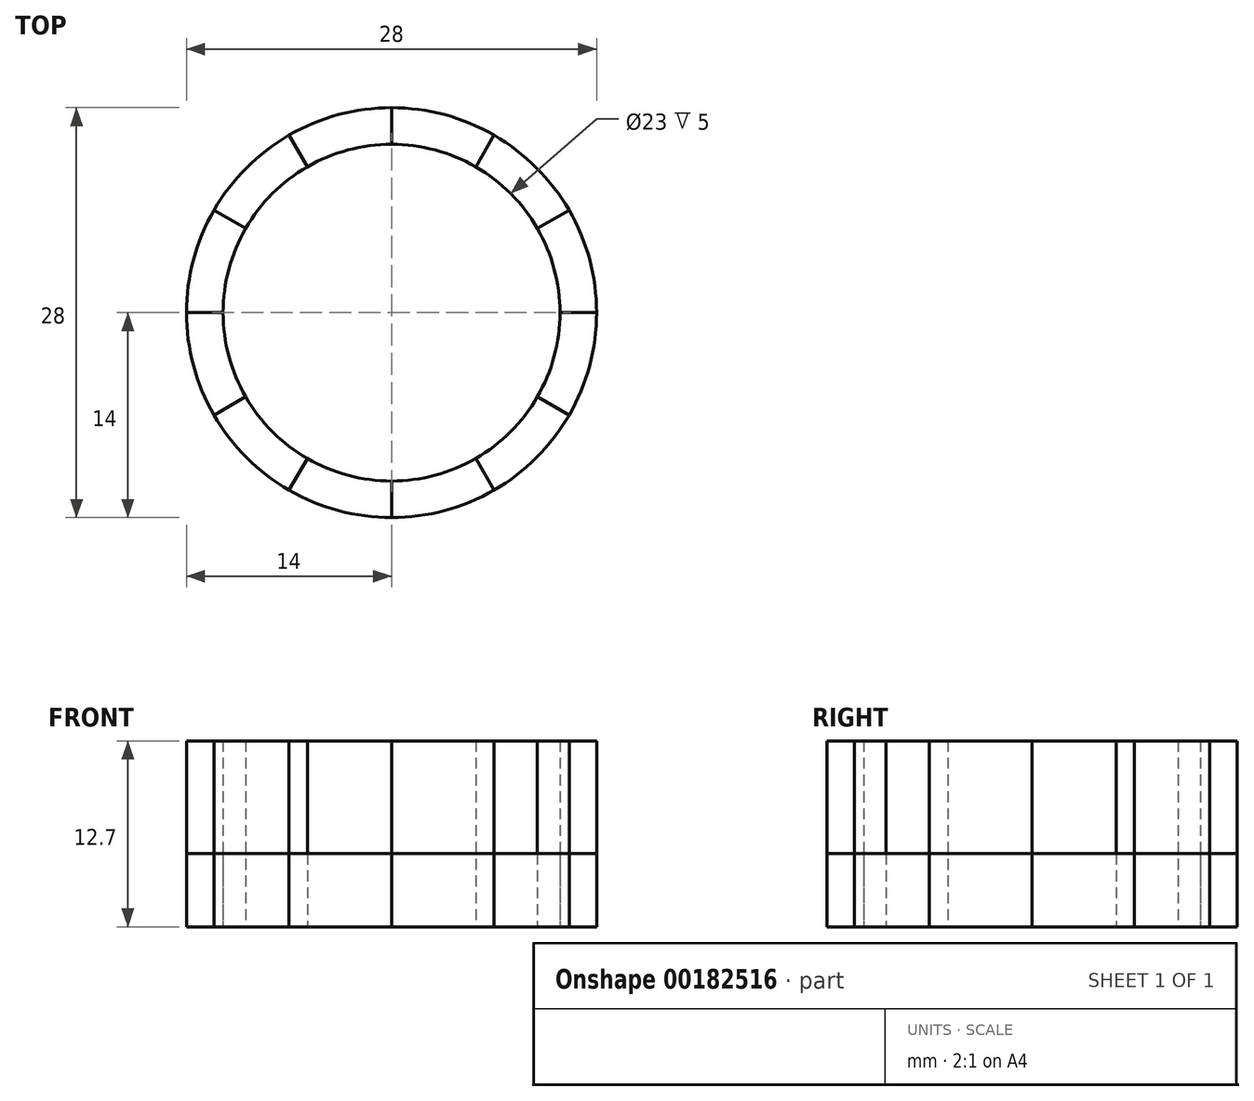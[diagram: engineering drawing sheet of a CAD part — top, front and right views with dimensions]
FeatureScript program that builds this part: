
annotation { "Feature Type Name" : "Feature", "Feature Type Description" : "" }
export const myFeature = defineFeature(function(context is Context, id is Id, definition is map)
    precondition{}
    {
        {
            var Q0;
            Q0=qCreatedBy(makeId("Top.planeOp"),FACE);
            var sketch = newSketch(context, id + "F0", { "sketchPlane" : qUnion([Q0])});
            skCircle(sketch, "E0", {"center": v(0, 0) * mm, "radius": 14 * mm});
            skLineSegment(sketch, "E1", {"start": v(0, 0) * mm, "end": v(0, 14) * mm});
            skLineSegment(sketch, "E2", {"start": v(0, 0) * mm, "end": v(14, 0) * mm});
            skLineSegment(sketch, "E3", {"start": v(0, 0) * mm, "end": v(0, -14) * mm});
            skLineSegment(sketch, "E4", {"start": v(0, 0) * mm, "end": v(-14, 0) * mm});
            skLineSegment(sketch, "E5", {"start": v(0, 0) * mm, "end": v(-7, 12.12) * mm});
            skLineSegment(sketch, "E6", {"start": v(0, 0) * mm, "end": v(-12.12, 7) * mm});
            skLineSegment(sketch, "E7", {"start": v(0, 0) * mm, "end": v(-12.12, -7) * mm});
            skLineSegment(sketch, "E8", {"start": v(0, 0) * mm, "end": v(-7, -12.12) * mm});
            skLineSegment(sketch, "E9", {"start": v(0, 0) * mm, "end": v(7, -12.12) * mm});
            skLineSegment(sketch, "E10", {"start": v(0, 0) * mm, "end": v(12.12, -7) * mm});
            skLineSegment(sketch, "E11", {"start": v(0, 0) * mm, "end": v(12.12, 7) * mm});
            skLineSegment(sketch, "E12", {"start": v(0, 0) * mm, "end": v(7, 12.12) * mm});
            skCircle(sketch, "E13", {"center": v(0, 0) * mm, "radius": 11.5 * mm});
            skSolve(sketch);
        }
        {
            var Q0;
            {var subQ0=sQuery(id+"F0.wireOp",EDGE,"E1");var subQ1=sQuery(id+"F0.wireOp",EDGE,"E0");var subQ2=makeQuery(id+"F0.imprint","INTERSECT",VERTEX,{"derivedFrom":[subQ1,subQ0]});Q0=makeQuery(id+"F0.imprint","IMPRINT",FACE,{"disambiguationData":[TD([[makeQuery(id+"F0.imprint","IMPRINT",EDGE,{"disambiguationData":[TD([[subQ2,-1.0]])],"derivedFrom":subQ1}),1.0]])]});}
            var Q1;
            {var subQ0=sQuery(id+"F0.wireOp",EDGE,"E4");var subQ1=sQuery(id+"F0.wireOp",EDGE,"E0");var subQ2=makeQuery(id+"F0.imprint","INTERSECT",VERTEX,{"derivedFrom":[subQ1,subQ0]});Q1=makeQuery(id+"F0.imprint","IMPRINT",FACE,{"disambiguationData":[TD([[makeQuery(id+"F0.imprint","IMPRINT",EDGE,{"disambiguationData":[TD([[subQ2,1.0]])],"derivedFrom":subQ1}),1.0]])]});}
            var Q2;
            {var subQ0=sQuery(id+"F0.wireOp",EDGE,"E11");var subQ1=sQuery(id+"F0.wireOp",EDGE,"E0");var subQ2=makeQuery(id+"F0.imprint","INTERSECT",VERTEX,{"derivedFrom":[subQ1,subQ0]});Q2=makeQuery(id+"F0.imprint","IMPRINT",FACE,{"disambiguationData":[TD([[makeQuery(id+"F0.imprint","IMPRINT",EDGE,{"disambiguationData":[TD([[subQ2,-1.0]])],"derivedFrom":subQ1}),1.0]])]});}
            var Q3;
            {var subQ0=sQuery(id+"F0.wireOp",EDGE,"E2");var subQ1=sQuery(id+"F0.wireOp",EDGE,"E0");var subQ2=makeQuery(id+"F0.imprint","INTERSECT",VERTEX,{"derivedFrom":[subQ1,subQ0]});Q3=makeQuery(id+"F0.imprint","IMPRINT",FACE,{"disambiguationData":[TD([[makeQuery(id+"F0.imprint","IMPRINT",EDGE,{"disambiguationData":[TD([[subQ2,1.0]])],"derivedFrom":subQ1}),1.0]])]});}
            var Q4;
            {var subQ0=sQuery(id+"F0.wireOp",EDGE,"E3");var subQ1=sQuery(id+"F0.wireOp",EDGE,"E0");var subQ2=makeQuery(id+"F0.imprint","INTERSECT",VERTEX,{"derivedFrom":[subQ1,subQ0]});Q4=makeQuery(id+"F0.imprint","IMPRINT",FACE,{"disambiguationData":[TD([[makeQuery(id+"F0.imprint","IMPRINT",EDGE,{"disambiguationData":[TD([[subQ2,-1.0]])],"derivedFrom":subQ1}),1.0]])]});}
            var Q5;
            {var subQ0=sQuery(id+"F0.wireOp",EDGE,"E7");var subQ1=sQuery(id+"F0.wireOp",EDGE,"E0");var subQ2=makeQuery(id+"F0.imprint","INTERSECT",VERTEX,{"derivedFrom":[subQ1,subQ0]});Q5=makeQuery(id+"F0.imprint","IMPRINT",FACE,{"disambiguationData":[TD([[makeQuery(id+"F0.imprint","IMPRINT",EDGE,{"disambiguationData":[TD([[subQ2,-1.0]])],"derivedFrom":subQ1}),1.0]])]});}
            extrude(context, id + "F1", {"entities" : qUnion([Q0, Q1, Q2, Q3, Q4, Q5]), "depth" : 12.7 * mm});
        }
        {
            var Q0;
            Q0 = qSketchRegion(id + "F0", true);
            extrude(context, id + "F2", {"entities" : qUnion([Q0]), "depth" : 5 * mm});
        }
    });
